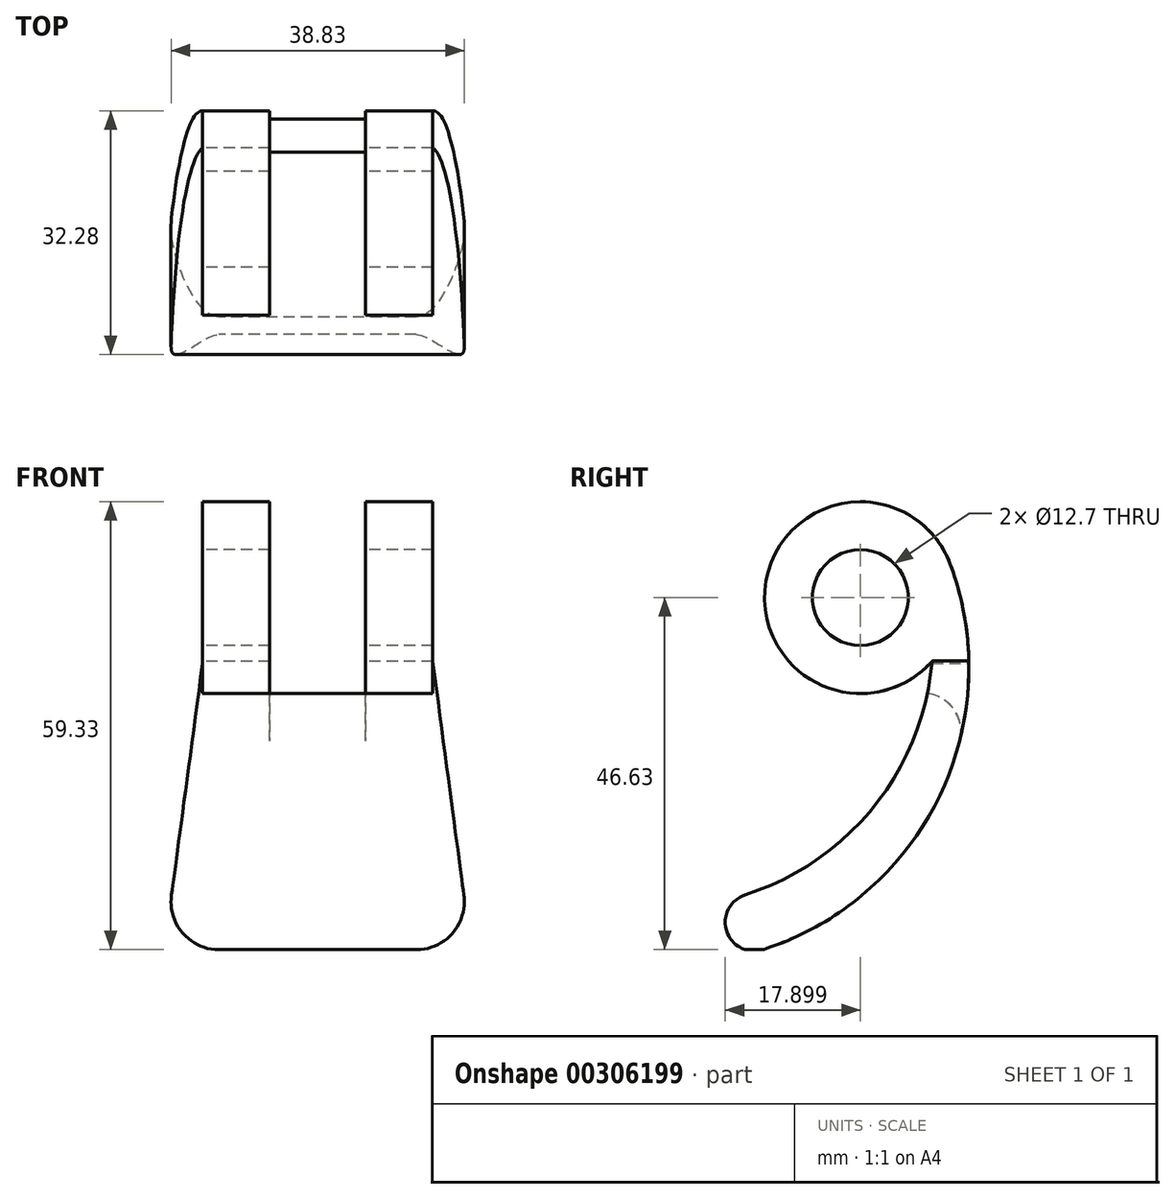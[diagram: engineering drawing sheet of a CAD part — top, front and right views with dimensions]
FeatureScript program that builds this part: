
annotation { "Feature Type Name" : "Feature", "Feature Type Description" : "" }
export const myFeature = defineFeature(function(context is Context, id is Id, definition is map)
    precondition{}
    {
        {
            var Q0;
            Q0=qCreatedBy(makeId("Front.planeOp"),FACE);
            var sketch = newSketch(context, id + "F0", { "sketchPlane" : qUnion([Q0])});
            skCircle(sketch, "E0", {"center": v(0, 0) * mm, "radius": 12.7 * mm});
            skCircle(sketch, "E1", {"center": v(0, 0) * mm, "radius": 6.35 * mm});
            skSolve(sketch);
        }
        {
            var Q0;
            Q0=qSketchRegion(id+"F0",true);
            extrude(context, id + "F1", {"entities" : qUnion([Q0]), "depth" : 30.48 * mm, "symmetric" : true});
        }
        {
            var Q0;
            Q0=qCreatedBy(makeId("Front.planeOp"),FACE);
            var sketch = newSketch(context, id + "F2", { "sketchPlane" : qUnion([Q0])});
            skArc(sketch, "E2", {"start": v(-12.94, -46.63) * mm, "mid": v(10.43, -26.42) * mm, "end": v(11.9, 4.44) * mm});
            skArc(sketch, "E3", {"start": v(-15.24, -39.37) * mm, "mid": v(1.83, -27.66) * mm, "end": v(9.5, -8.43) * mm});
            skArc(sketch, "E4", {"start": v(-15.24, -39.37) * mm, "mid": v(-17.73, -44.15) * mm, "end": v(-12.94, -46.63) * mm});
            skArc(sketch, "E5", {"start": v(9.5, -8.43) * mm, "mid": v(12.48, -2.33) * mm, "end": v(11.9, 4.44) * mm});
            skSolve(sketch);
        }
        {
            var Q0;
            Q0=qSketchRegion(id+"F2",true);
            extrude(context, id + "F3", {"entities" : qUnion([Q0]), "operationType" : NewBodyOperationType.ADD, "depth" : 40.64 * mm, "symmetric" : true});
        }
        {
            var Q0;
            Q0=qCreatedBy(makeId("Front.planeOp"),FACE);
            var sketch = newSketch(context, id + "F4", { "sketchPlane" : qUnion([Q0])});
            skCircle(sketch, "E6", {"center": v(0, 0) * mm, "radius": 12.7 * mm});
            skSolve(sketch);
        }
        {
            var Q0;
            Q0=qSketchRegion(id+"F4",true);
            extrude(context, id + "F5", {"entities" : qUnion([Q0]), "operationType" : NewBodyOperationType.REMOVE, "depth" : 12.7 * mm, "symmetric" : true});
        }
        {
            var Q0;
            Q0=qCreatedBy(makeId("Right.planeOp"),FACE);
            var sketch = newSketch(context, id + "F6", { "sketchPlane" : qUnion([Q0])});
            skLineSegment(sketch, "E7.bottom", {"start": v(-6.35, 12.7) * mm, "end": v(6.35, 12.7) * mm});
            skLineSegment(sketch, "E7.top", {"start": v(-6.35, -12.7) * mm, "end": v(6.35, -12.7) * mm});
            skLineSegment(sketch, "E7.left", {"start": v(-6.35, 12.7) * mm, "end": v(-6.35, -12.7) * mm});
            skLineSegment(sketch, "E7.right", {"start": v(6.35, 12.7) * mm, "end": v(6.35, -12.7) * mm});
            skSolve(sketch);
        }
        {
            var Q0;
            Q0=qSketchRegion(id+"F6",true);
            extrude(context, id + "F7", {"entities" : qUnion([Q0]), "operationType" : NewBodyOperationType.REMOVE, "endBound" : BoundingType.THROUGH_ALL, "depth" : 25.4 * mm});
        }
        {
            var Q0;
            Q0=makeQuery(id+"F7.boolean.opBoolean","INTERSECT",EDGE,{"derivedFrom":[makeQuery(id+"F3.opExtrude","SWEPT_FACE",FACE,{"disambiguationData":[OSD([sQuery(id+"F2.wireOp",EDGE,"E2")])]}),makeQuery(id+"F7.opExtrude","SWEPT_FACE",FACE,{"disambiguationData":[OSD([sQuery(id+"F6.wireOp",EDGE,"E7.top")])]})]});
            fillet(context, id + "F8", {"entities" : qUnion([Q0]), "radius" : 5.08 * mm, "tangentPropagation" : true, "allowEdgeOverflow" : false});
        }
        {
            var Q0;
            Q0=qCreatedBy(makeId("Right.planeOp"),FACE);
            var sketch = newSketch(context, id + "F9", { "sketchPlane" : qUnion([Q0])});
            skLineSegment(sketch, "E8", {"start": v(0, 0) * mm, "end": v(0, 34.87) * mm, "construction": true});
            skSolve(sketch);
        }
        {
            var Q0;
            Q0=makeQuery(id+"F1.opExtrude","SWEPT_BODY",BODY,{"disambiguationData":[OSD([sQuery(id+"F0.wireOp",EDGE,"E0"),sQuery(id+"F0.wireOp",EDGE,"E1")])]});
            var Q1;
            Q1=sQuery(id+"F9.wireOp",EDGE,"E8");
            transform(context, id + "F10", {"entities" : qUnion([Q0]), "transformType" : TransformType.ROTATION, "transformAxis" : qUnion([Q1]), "angle" : 1.57 * radian, "makeCopy" : false});
        }
        {
            var Q0;
            Q0=qCreatedBy(makeId("Front.planeOp"),FACE);
            var sketch = newSketch(context, id + "F11", { "sketchPlane" : qUnion([Q0])});
            skLineSegment(sketch, "E9", {"start": v(15.24, -8.38) * mm, "end": v(19.37, -39.45) * mm});
            skLineSegment(sketch, "E10", {"start": v(13.07, -46.63) * mm, "end": v(-13.06, -46.63) * mm});
            skLineSegment(sketch, "E11", {"start": v(-19.36, -39.44) * mm, "end": v(-15.24, -8.7) * mm});
            skLineSegment(sketch, "E12", {"start": v(-15.24, -8.7) * mm, "end": v(-15.24, 12.7) * mm});
            skLineSegment(sketch, "E13", {"start": v(-15.24, 12.7) * mm, "end": v(15.24, 12.7) * mm});
            skLineSegment(sketch, "E14", {"start": v(15.24, 12.7) * mm, "end": v(15.24, -8.38) * mm});
            skPoint(sketch, "E15.visualSharp", {"position": v(20.32, -46.63) * mm});
            skArc(sketch, "E15.filletArc", {"start": v(13.07, -46.63) * mm, "mid": v(17.85, -44.47) * mm, "end": v(19.37, -39.45) * mm});
            skPoint(sketch, "E16.visualSharp", {"position": v(-20.32, -46.63) * mm});
            skArc(sketch, "E16.filletArc", {"start": v(-19.36, -39.44) * mm, "mid": v(-17.84, -44.47) * mm, "end": v(-13.06, -46.63) * mm});
            skSolve(sketch);
        }
        {
            var Q0;
            Q0=qSketchRegion(id+"F11",true);
            extrude(context, id + "F12", {"entities" : qUnion([Q0]), "operationType" : NewBodyOperationType.INTERSECT, "depth" : 76.2 * mm, "symmetric" : true});
        }
    });
